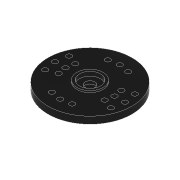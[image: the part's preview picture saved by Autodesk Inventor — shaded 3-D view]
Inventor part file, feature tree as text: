
AUTODESK INVENTOR PART (.ipt)
format: ipt  version: 2022 (Build 260153000, 153)  size: 194,560 bytes
history: native  units: mm
features: sketch x8, extrude x6, hole x2
ambient origin geometry x8: Origin, YZ Plane, XZ Plane, XY Plane, X Axis, Y Axis, Z Axis, Center Point
bodies: Solid1 (feature_tree)
feature tree (16):
  extrude  "Extrusion1"  Depth=2.0mm TaperAngle=0.0deg
  extrude  "Extrusion2"  Depth=2.5mm TaperAngle=0.0deg
  extrude  "Extrusion3"  Depth=3.0mm TaperAngle=0.0deg
  extrude  "Extrusion4"  Depth=0.5mm TaperAngle=0.0deg
  extrude  "Extrusion5"  Depth=1.2mm TaperAngle=0.0deg
  extrude  "Extrusion6"  Depth=1.2mm TaperAngle=0.0deg
  hole  "Hole1"  [1 undecoded]
  hole  "Hole2"  [1 undecoded]
  sketch  "Sketch1"  dims[d0=24.0mm d1=2.0mm d2=0.0mm]
  sketch  "Sketch2"  dims[d3=9.0mm d4=2.5mm d5=0.0mm]
  sketch  "Sketch3"  dims[d6=5.8mm d7=3.0mm d8=0.0mm]
  sketch  "Sketch4"  dims[d9=7.5mm d10=0.5mm d11=0.0mm]
  sketch  "Sketch5"  dims[d12=6.0mm d13=1.2mm d14=0.0mm]
  sketch  "Sketch6"  dims[d15=2.8mm d16=1.2mm d17=0.0mm]
  sketch  "Sketch7"  dims[d18=17.0mm d20=3.490659mm]
  sketch  "Sketch8"  dims[d21=1.5mm d22=6.0mm d23=4.0mm d24=2.0mm d25=90.0deg d26=8.0mm d27=20.594885mm d28=20.0mm d30=6.981317mm d31=14.0mm d32=1.5mm d33=6.0mm d34=4.0mm d35=2.0mm d36=90.0deg d37=8.0mm d38=20.594885mm]
note: 2 required parameter values undecoded (feature->parameter linkage not recoverable at this tier; creation-order binding heuristic only, values carry confidence <= 0.55)
